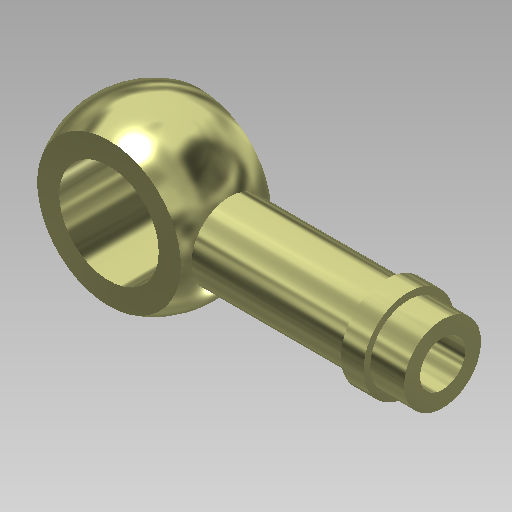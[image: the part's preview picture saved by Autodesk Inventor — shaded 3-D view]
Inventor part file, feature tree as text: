
AUTODESK INVENTOR PART (.ipt)
format: ipt  version: 2018.1 (Build 221171000, 171)  size: 196,608 bytes
history: native  units: in
note: dims shown in document units (in); Inventor stores cm internally (conversion verified against a paired STEP export)
features: sketch x5, extrude x3, revolve x2
ambient origin geometry x8: Origin, YZ Plane, XZ Plane, XY Plane, X Axis, Y Axis, Z Axis, Center Point
bodies: Body1 (feature_tree)
feature tree (10):
  revolve  "Revolution2"  [1 undecoded]
  extrude  "Extrusion1"  Depth=0.1969in TaperAngle=0.0deg
  extrude  "Extrusion2"  Depth=0.0787in
  revolve  "Revolution3"  [1 undecoded]
  extrude  "Extrusion3"  [1 undecoded]
  sketch  "Sketch2"  dims[d3=90.0deg d6=0.3937in d7=0.0in]
  sketch  "Sketch3"  dims[d8=0.1732in d9=0.1969in d10=0.0in]
  sketch  "Sketch4"  dims[d16=90.0deg d17=0.0787in]
  sketch  "Sketch5"  dims[d18=0.4724in d19=0.0in]
  sketch  "Sketch6"
note: 3 required parameter values undecoded (feature->parameter linkage not recoverable at this tier; creation-order binding heuristic only, values carry confidence <= 0.55)